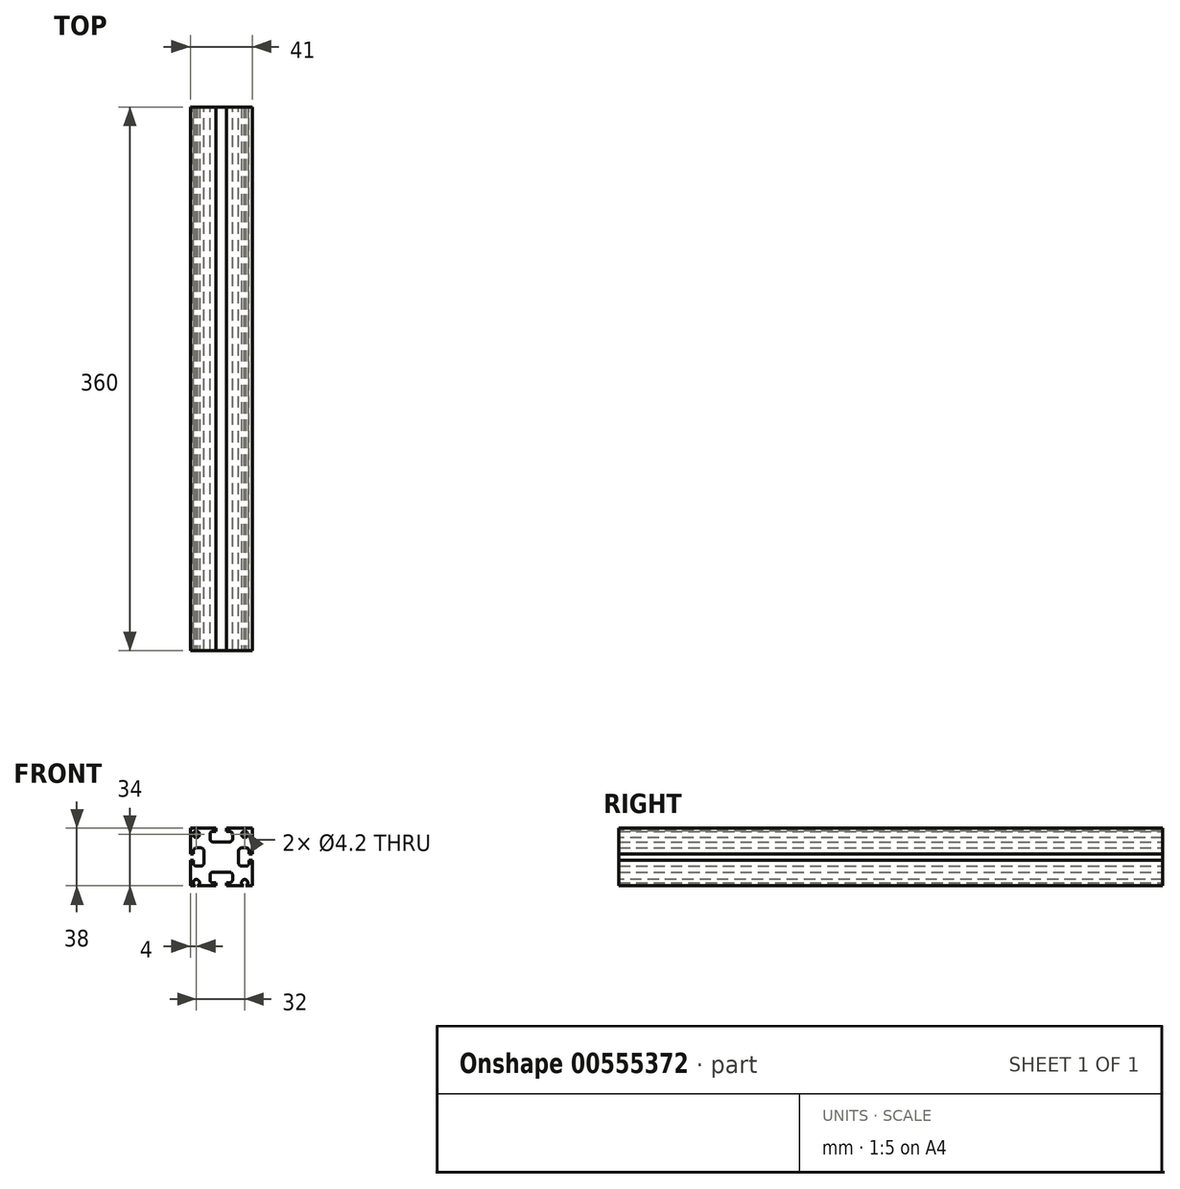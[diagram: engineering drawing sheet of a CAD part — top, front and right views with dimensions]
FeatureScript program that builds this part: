
annotation { "Feature Type Name" : "Feature", "Feature Type Description" : "" }
export const myFeature = defineFeature(function(context is Context, id is Id, definition is map)
    precondition{}
    {
        {
            var Q0;
            Q0=qCreatedBy(makeId("Front.planeOp"),FACE);
            var sketch = newSketch(context, id + "F0", { "sketchPlane" : qUnion([Q0])});
            skLineSegment(sketch, "E0", {"start": v(0, 0) * mm, "end": v(0, 10) * mm});
            skLineSegment(sketch, "E1", {"start": v(0, 10) * mm, "end": v(-7.5, 10) * mm});
            skLineSegment(sketch, "E2", {"start": v(-7.5, 10) * mm, "end": v(-7.5, 17) * mm});
            skLineSegment(sketch, "E3", {"start": v(-7.5, 17) * mm, "end": v(-3.5, 17) * mm});
            skLineSegment(sketch, "E4", {"start": v(-3.5, 17) * mm, "end": v(-3.5, 19) * mm});
            skLineSegment(sketch, "E5", {"start": v(-3.5, 19) * mm, "end": v(-20.5, 19) * mm});
            skLineSegment(sketch, "E6", {"start": v(-20.5, 19) * mm, "end": v(-20.5, 2) * mm});
            skLineSegment(sketch, "E7", {"start": v(-20.5, 2) * mm, "end": v(-18.5, 2) * mm});
            skLineSegment(sketch, "E8", {"start": v(-18.5, 2) * mm, "end": v(-18.5, 6) * mm});
            skLineSegment(sketch, "E9", {"start": v(-18.5, 6) * mm, "end": v(-11.5, 6) * mm});
            skLineSegment(sketch, "E10", {"start": v(-11.5, 6) * mm, "end": v(-11.5, 0) * mm});
            skLineSegment(sketch, "E11.MirrorCS", {"start": v(-3.5, -19) * mm, "end": v(-20.5, -19) * mm});
            skLineSegment(sketch, "E12.MirrorCS", {"start": v(-20.5, -19) * mm, "end": v(-20.5, -2) * mm});
            skLineSegment(sketch, "E13.MirrorCS", {"start": v(-18.5, -2) * mm, "end": v(-18.5, -6) * mm});
            skLineSegment(sketch, "E14.MirrorCS", {"start": v(-18.5, -6) * mm, "end": v(-11.5, -6) * mm});
            skLineSegment(sketch, "E15.MirrorCS", {"start": v(-11.5, -6) * mm, "end": v(-11.5, 0) * mm});
            skLineSegment(sketch, "E16.MirrorCS", {"start": v(0, 0) * mm, "end": v(0, -10) * mm});
            skLineSegment(sketch, "E17.MirrorCS", {"start": v(0, -10) * mm, "end": v(-7.5, -10) * mm});
            skLineSegment(sketch, "E18.MirrorCS", {"start": v(-7.5, -10) * mm, "end": v(-7.5, -17) * mm});
            skLineSegment(sketch, "E19.MirrorCS", {"start": v(-7.5, -17) * mm, "end": v(-3.5, -17) * mm});
            skLineSegment(sketch, "E20.MirrorCS", {"start": v(-3.5, -17) * mm, "end": v(-3.5, -19) * mm});
            skLineSegment(sketch, "E21.MirrorCS", {"start": v(-20.5, -2) * mm, "end": v(-18.5, -2) * mm});
            skLineSegment(sketch, "E22.MirrorCS", {"start": v(0, -10) * mm, "end": v(7.5, -10) * mm});
            skLineSegment(sketch, "E23.MirrorCS", {"start": v(7.5, -10) * mm, "end": v(7.5, -17) * mm});
            skLineSegment(sketch, "E24.MirrorCS", {"start": v(7.5, -17) * mm, "end": v(3.5, -17) * mm});
            skLineSegment(sketch, "E25.MirrorCS", {"start": v(3.5, -19) * mm, "end": v(20.5, -19) * mm});
            skLineSegment(sketch, "E26.MirrorCS", {"start": v(20.5, -19) * mm, "end": v(20.5, -2) * mm});
            skLineSegment(sketch, "E27.MirrorCS", {"start": v(3.5, -17) * mm, "end": v(3.5, -19) * mm});
            skLineSegment(sketch, "E28.MirrorCS", {"start": v(0, 10) * mm, "end": v(7.5, 10) * mm});
            skLineSegment(sketch, "E29.MirrorCS", {"start": v(7.5, 10) * mm, "end": v(7.5, 17) * mm});
            skLineSegment(sketch, "E30.MirrorCS", {"start": v(7.5, 17) * mm, "end": v(3.5, 17) * mm});
            skLineSegment(sketch, "E31.MirrorCS", {"start": v(3.5, 17) * mm, "end": v(3.5, 19) * mm});
            skLineSegment(sketch, "E32.MirrorCS", {"start": v(3.5, 19) * mm, "end": v(20.5, 19) * mm});
            skLineSegment(sketch, "E33.MirrorCS", {"start": v(20.5, 19) * mm, "end": v(20.5, 2) * mm});
            skLineSegment(sketch, "E34.MirrorCS", {"start": v(18.5, 2) * mm, "end": v(18.5, 6) * mm});
            skLineSegment(sketch, "E35.MirrorCS", {"start": v(18.5, 6) * mm, "end": v(11.5, 6) * mm});
            skLineSegment(sketch, "E36.MirrorCS", {"start": v(11.5, 6) * mm, "end": v(11.5, 0) * mm});
            skLineSegment(sketch, "E37.MirrorCS", {"start": v(11.5, -6) * mm, "end": v(11.5, 0) * mm});
            skLineSegment(sketch, "E38.MirrorCS", {"start": v(18.5, -6) * mm, "end": v(11.5, -6) * mm});
            skLineSegment(sketch, "E39.MirrorCS", {"start": v(18.5, -2) * mm, "end": v(18.5, -6) * mm});
            skLineSegment(sketch, "E40.MirrorCS", {"start": v(20.5, -2) * mm, "end": v(18.5, -2) * mm});
            skLineSegment(sketch, "E41.MirrorCS", {"start": v(20.5, 2) * mm, "end": v(18.5, 2) * mm});
            skSolve(sketch);
        }
        {
            var Q0;
            Q0=makeQuery(id+"F0.imprint","IMPRINT",FACE,{"disambiguationData":[TD([[makeQuery(id+"F0.imprint","IMPRINT",EDGE,{"derivedFrom":sQuery(id+"F0.wireOp",EDGE,"E0")}),1.0]])]});
            var Q1;
            Q1=makeQuery(id+"F0.imprint","IMPRINT",FACE,{"disambiguationData":[TD([[makeQuery(id+"F0.imprint","IMPRINT",EDGE,{"derivedFrom":sQuery(id+"F0.wireOp",EDGE,"E0")}),-1.0]])]});
            extrude(context, id + "F1", {"entities" : qUnion([Q0, Q1]), "depth" : 360 * mm, "offsetDistance" : 25 * mm});
        }
        {
            var Q0;
            Q0=makeQuery(id+"F1.opExtrude","CAP_FACE",FACE,{"disambiguationData":[OSD([sQuery(id+"F0.wireOp",EDGE,"E1"),sQuery(id+"F0.wireOp",EDGE,"E2"),sQuery(id+"F0.wireOp",EDGE,"E3"),sQuery(id+"F0.wireOp",EDGE,"E4"),sQuery(id+"F0.wireOp",EDGE,"E5"),sQuery(id+"F0.wireOp",EDGE,"E6"),sQuery(id+"F0.wireOp",EDGE,"E7"),sQuery(id+"F0.wireOp",EDGE,"E8"),sQuery(id+"F0.wireOp",EDGE,"E9"),sQuery(id+"F0.wireOp",EDGE,"E10"),sQuery(id+"F0.wireOp",EDGE,"E11.MirrorCS"),sQuery(id+"F0.wireOp",EDGE,"E12.MirrorCS"),sQuery(id+"F0.wireOp",EDGE,"E13.MirrorCS"),sQuery(id+"F0.wireOp",EDGE,"E14.MirrorCS"),sQuery(id+"F0.wireOp",EDGE,"E15.MirrorCS"),sQuery(id+"F0.wireOp",EDGE,"E17.MirrorCS"),sQuery(id+"F0.wireOp",EDGE,"E18.MirrorCS"),sQuery(id+"F0.wireOp",EDGE,"E19.MirrorCS"),sQuery(id+"F0.wireOp",EDGE,"E20.MirrorCS"),sQuery(id+"F0.wireOp",EDGE,"E21.MirrorCS"),sQuery(id+"F0.wireOp",EDGE,"E22.MirrorCS"),sQuery(id+"F0.wireOp",EDGE,"E23.MirrorCS"),sQuery(id+"F0.wireOp",EDGE,"E24.MirrorCS"),sQuery(id+"F0.wireOp",EDGE,"E25.MirrorCS"),sQuery(id+"F0.wireOp",EDGE,"E26.MirrorCS"),sQuery(id+"F0.wireOp",EDGE,"E27.MirrorCS"),sQuery(id+"F0.wireOp",EDGE,"E28.MirrorCS"),sQuery(id+"F0.wireOp",EDGE,"E29.MirrorCS"),sQuery(id+"F0.wireOp",EDGE,"E30.MirrorCS"),sQuery(id+"F0.wireOp",EDGE,"E31.MirrorCS"),sQuery(id+"F0.wireOp",EDGE,"E32.MirrorCS"),sQuery(id+"F0.wireOp",EDGE,"E33.MirrorCS"),sQuery(id+"F0.wireOp",EDGE,"E34.MirrorCS"),sQuery(id+"F0.wireOp",EDGE,"E35.MirrorCS"),sQuery(id+"F0.wireOp",EDGE,"E36.MirrorCS"),sQuery(id+"F0.wireOp",EDGE,"E37.MirrorCS"),sQuery(id+"F0.wireOp",EDGE,"E38.MirrorCS"),sQuery(id+"F0.wireOp",EDGE,"E39.MirrorCS"),sQuery(id+"F0.wireOp",EDGE,"E40.MirrorCS"),sQuery(id+"F0.wireOp",EDGE,"E41.MirrorCS")])],"isStart":false});
            var sketch = newSketch(context, id + "F2", { "sketchPlane" : qUnion([Q0])});
            skPoint(sketch, "E42", {"position": v(-16.5, 15) * mm});
            skPoint(sketch, "E43", {"position": v(-16.5, -17) * mm});
            skPoint(sketch, "E44", {"position": v(15.5, -17) * mm});
            skPoint(sketch, "E45", {"position": v(15.5, 15) * mm});
            skSolve(sketch);
        }
        {
            var Q0;
            Q0=sQuery(id+"F2.wireOp",VERTEX,"E45");
            var Q1;
            Q1=sQuery(id+"F2.wireOp",VERTEX,"E42");
            var Q2;
            Q2=sQuery(id+"F2.wireOp",VERTEX,"E44");
            var Q3;
            Q3=sQuery(id+"F2.wireOp",VERTEX,"E43");
            var Q4;
            Q4=makeQuery(id+"F1.opExtrude","SWEPT_BODY",BODY,{"disambiguationData":[OSD([sQuery(id+"F0.wireOp",EDGE,"E1"),sQuery(id+"F0.wireOp",EDGE,"E2"),sQuery(id+"F0.wireOp",EDGE,"E3"),sQuery(id+"F0.wireOp",EDGE,"E4"),sQuery(id+"F0.wireOp",EDGE,"E5"),sQuery(id+"F0.wireOp",EDGE,"E6"),sQuery(id+"F0.wireOp",EDGE,"E7"),sQuery(id+"F0.wireOp",EDGE,"E8"),sQuery(id+"F0.wireOp",EDGE,"E9"),sQuery(id+"F0.wireOp",EDGE,"E10"),sQuery(id+"F0.wireOp",EDGE,"E11.MirrorCS"),sQuery(id+"F0.wireOp",EDGE,"E12.MirrorCS"),sQuery(id+"F0.wireOp",EDGE,"E13.MirrorCS"),sQuery(id+"F0.wireOp",EDGE,"E14.MirrorCS"),sQuery(id+"F0.wireOp",EDGE,"E15.MirrorCS"),sQuery(id+"F0.wireOp",EDGE,"E17.MirrorCS"),sQuery(id+"F0.wireOp",EDGE,"E18.MirrorCS"),sQuery(id+"F0.wireOp",EDGE,"E19.MirrorCS"),sQuery(id+"F0.wireOp",EDGE,"E20.MirrorCS"),sQuery(id+"F0.wireOp",EDGE,"E21.MirrorCS"),sQuery(id+"F0.wireOp",EDGE,"E22.MirrorCS"),sQuery(id+"F0.wireOp",EDGE,"E23.MirrorCS"),sQuery(id+"F0.wireOp",EDGE,"E24.MirrorCS"),sQuery(id+"F0.wireOp",EDGE,"E25.MirrorCS"),sQuery(id+"F0.wireOp",EDGE,"E26.MirrorCS"),sQuery(id+"F0.wireOp",EDGE,"E27.MirrorCS"),sQuery(id+"F0.wireOp",EDGE,"E28.MirrorCS"),sQuery(id+"F0.wireOp",EDGE,"E29.MirrorCS"),sQuery(id+"F0.wireOp",EDGE,"E30.MirrorCS"),sQuery(id+"F0.wireOp",EDGE,"E31.MirrorCS"),sQuery(id+"F0.wireOp",EDGE,"E32.MirrorCS"),sQuery(id+"F0.wireOp",EDGE,"E33.MirrorCS"),sQuery(id+"F0.wireOp",EDGE,"E34.MirrorCS"),sQuery(id+"F0.wireOp",EDGE,"E35.MirrorCS"),sQuery(id+"F0.wireOp",EDGE,"E36.MirrorCS"),sQuery(id+"F0.wireOp",EDGE,"E37.MirrorCS"),sQuery(id+"F0.wireOp",EDGE,"E38.MirrorCS"),sQuery(id+"F0.wireOp",EDGE,"E39.MirrorCS"),sQuery(id+"F0.wireOp",EDGE,"E40.MirrorCS"),sQuery(id+"F0.wireOp",EDGE,"E41.MirrorCS")])]});
            hole(context, id + "F3", {"style" : HoleStyle.SIMPLE, "endStyle" : HoleEndStyle.THROUGH, "standardTappedOrClearance" : lookupTablePath({ "standard" : "ISO", "engagement" : "75%", "pitch" : "0.8 mm", "size" : "M5", "type" : "Tapped" }), "standardBlindInLast" : lookupTablePath({ "standard" : "ISO", "engagement" : "75%", "pitch" : "0.8 mm", "size" : "M5", "type" : "Tapped" }), "holeDiameter" : 4.2 * mm, "showTappedDepth" : true, "isTappedThrough" : true, "tappedDepth" : 8 * mm, "tapClearance" : 3, "startFromSketch" : true, "locations" : qUnion([Q0, Q1, Q2, Q3]), "scope" : qUnion([Q4]), "majorDiameter" : 5 * mm});
        }
        {
            var Q0;
            Q0=makeQuery(id+"F1.opExtrude","SWEPT_EDGE",EDGE,{"disambiguationData":[OSD([sQuery(id+"F0.wireOp",EDGE,"E1"),sQuery(id+"F0.wireOp",EDGE,"E2")])]});
            var Q1;
            Q1=makeQuery(id+"F1.opExtrude","SWEPT_EDGE",EDGE,{"disambiguationData":[OSD([sQuery(id+"F0.wireOp",EDGE,"E13.MirrorCS"),sQuery(id+"F0.wireOp",EDGE,"E14.MirrorCS")])]});
            var Q2;
            Q2=makeQuery(id+"F1.opExtrude","SWEPT_EDGE",EDGE,{"disambiguationData":[OSD([sQuery(id+"F0.wireOp",EDGE,"E18.MirrorCS"),sQuery(id+"F0.wireOp",EDGE,"E19.MirrorCS")])]});
            var Q3;
            Q3=makeQuery(id+"F1.opExtrude","SWEPT_EDGE",EDGE,{"disambiguationData":[OSD([sQuery(id+"F0.wireOp",EDGE,"E37.MirrorCS"),sQuery(id+"F0.wireOp",EDGE,"E38.MirrorCS")])]});
            fillet(context, id + "F4", {"entities" : qUnion([Q0, Q1, Q2, Q3]), "radius" : 2 * mm, "tangentPropagation" : true, "allowEdgeOverflow" : false});
        }
        {
            var Q0;
            Q0=makeQuery(id+"F1.opExtrude","SWEPT_EDGE",EDGE,{"disambiguationData":[OSD([sQuery(id+"F0.wireOp",EDGE,"E28.MirrorCS"),sQuery(id+"F0.wireOp",EDGE,"E29.MirrorCS")])]});
            fillet(context, id + "F5", {"entities" : qUnion([Q0]), "radius" : 2 * mm, "tangentPropagation" : true, "allowEdgeOverflow" : false});
        }
        {
            var Q0;
            Q0=makeQuery(id+"F1.opExtrude","SWEPT_EDGE",EDGE,{"disambiguationData":[OSD([sQuery(id+"F0.wireOp",EDGE,"E14.MirrorCS"),sQuery(id+"F0.wireOp",EDGE,"E15.MirrorCS")])]});
            var Q1;
            Q1=makeQuery(id+"F1.opExtrude","SWEPT_EDGE",EDGE,{"disambiguationData":[OSD([sQuery(id+"F0.wireOp",EDGE,"E22.MirrorCS"),sQuery(id+"F0.wireOp",EDGE,"E23.MirrorCS")])]});
            var Q2;
            Q2=makeQuery(id+"F1.opExtrude","SWEPT_EDGE",EDGE,{"disambiguationData":[OSD([sQuery(id+"F0.wireOp",EDGE,"E34.MirrorCS"),sQuery(id+"F0.wireOp",EDGE,"E35.MirrorCS")])]});
            fillet(context, id + "F6", {"entities" : qUnion([Q0, Q1, Q2]), "radius" : 2 * mm, "tangentPropagation" : true, "allowEdgeOverflow" : false});
        }
        {
            var Q0;
            Q0=makeQuery(id+"F1.opExtrude","SWEPT_EDGE",EDGE,{"disambiguationData":[OSD([sQuery(id+"F0.wireOp",EDGE,"E23.MirrorCS"),sQuery(id+"F0.wireOp",EDGE,"E24.MirrorCS")])]});
            var Q1;
            Q1=makeQuery(id+"F1.opExtrude","SWEPT_EDGE",EDGE,{"disambiguationData":[OSD([sQuery(id+"F0.wireOp",EDGE,"E38.MirrorCS"),sQuery(id+"F0.wireOp",EDGE,"E39.MirrorCS")])]});
            fillet(context, id + "F7", {"entities" : qUnion([Q0, Q1]), "radius" : 2 * mm, "tangentPropagation" : true, "allowEdgeOverflow" : false});
        }
        {
            var Q0;
            Q0=makeQuery(id+"F1.opExtrude","SWEPT_EDGE",EDGE,{"disambiguationData":[OSD([sQuery(id+"F0.wireOp",EDGE,"E17.MirrorCS"),sQuery(id+"F0.wireOp",EDGE,"E18.MirrorCS")])]});
            var Q1;
            Q1=makeQuery(id+"F1.opExtrude","SWEPT_EDGE",EDGE,{"disambiguationData":[OSD([sQuery(id+"F0.wireOp",EDGE,"E8"),sQuery(id+"F0.wireOp",EDGE,"E9")])]});
            var Q2;
            Q2=makeQuery(id+"F1.opExtrude","SWEPT_EDGE",EDGE,{"disambiguationData":[OSD([sQuery(id+"F0.wireOp",EDGE,"E2"),sQuery(id+"F0.wireOp",EDGE,"E3")])]});
            var Q3;
            Q3=makeQuery(id+"F1.opExtrude","SWEPT_EDGE",EDGE,{"disambiguationData":[OSD([sQuery(id+"F0.wireOp",EDGE,"E35.MirrorCS"),sQuery(id+"F0.wireOp",EDGE,"E36.MirrorCS")])]});
            fillet(context, id + "F8", {"entities" : qUnion([Q0, Q1, Q2, Q3]), "radius" : 2 * mm, "tangentPropagation" : true, "allowEdgeOverflow" : false});
        }
        {
            var Q0;
            Q0=makeQuery(id+"F1.opExtrude","SWEPT_EDGE",EDGE,{"disambiguationData":[OSD([sQuery(id+"F0.wireOp",EDGE,"E9"),sQuery(id+"F0.wireOp",EDGE,"E10")])]});
            var Q1;
            Q1=makeQuery(id+"F1.opExtrude","SWEPT_EDGE",EDGE,{"disambiguationData":[OSD([sQuery(id+"F0.wireOp",EDGE,"E29.MirrorCS"),sQuery(id+"F0.wireOp",EDGE,"E30.MirrorCS")])]});
            fillet(context, id + "F9", {"entities" : qUnion([Q0, Q1]), "radius" : 2 * mm, "tangentPropagation" : true, "allowEdgeOverflow" : false});
        }
    });
